# Revit family: Domotics-DomesticRanges-GEWISS-SYSTEM_COMMAND-THREE-WAY_SWITCH
name_source: partatom
category: Apparecchi elettrici
revit_build: Autodesk Revit 2016 (Build: 20161004_0715(x64)
units: mm (PartAtom-declared; Revit-internal decimal feet)

## family parameters
Condiviso = Sì
Host = Superficie
Mantenere orientamento annotazione = Sì
Numero OmniClass = 23.80.50.11.14
Punto di calcolo locali = Sì
Quota connettore circolare = Usa diametro
Taglio con vuoti quando caricato = No
Tipo di parte = Normale
Titolo OmniClass = Switches

## types (5) — shared parameters
Bidimensionale = bidimensionale system commutatori : simboli
Carico apparente = 0 VA
Catalogue = DOMOTICS
Catalogue Range = SYSTEM - DOMESTIC RANGE
Description. = Three-way switch
Electrocod = 0130
IDF = dab08859-5c6b-41ac-be4a-f9753a63331f
IDT = c003c8fd-f059-4307-83ec-7b86c7d74ecb
Immagine tipo = GW21559.jpg
Larghezza pulsante = 23 mm  [stored 0.0754593 ft]
N. poli = 1
No. SYSTEM modules = 1
Produttore = GEWISS S.p.A.
Prospetto di default = 1219 mm
SEO = 3 way switch
Simbolo_ = SIMBOLO COMMUTATORI : COMM
Technical sheet = https://www.gewiss.com
Tipo_ = SYSTEM COMMUTATORI_BASE : GW21559 - Nero
URL = https://www.gewiss.com
Version file RFA = 19.4
Volt = 230 V

## per-type parameters (varying)
| type | Button key | Colour | Description: | Descrizione | EAN code | Modello | Type | Voltage | Voltage: |
| GW21559 - Black | Neutral | Black | 1P - 10AX | 3-WAY SWITCH 1-0-2 10A SY/BK | 8011564133082 | GW21559 | 1P | 250 V ac | 250 V ac |
| GW20559 - White | Neutral | White | 1P - 10AX | 3-WAY SWITCH 1-0-2 10A SY/WT | 8011564133006 | GW20559 | 1P | 250 V ac | 250 V ac |
| GW21528 - Black | With replaceable neutral lens | Black | 1P - 10AX | 3-WAY SWITCH 1-0-2 10A NEUT.DISCS SY/BK | 8011564128279 | GW21528 | 1P | 250 V ac | 250 V ac |
| GW20560 - White 2P | Neutral |  | 2P - 10AX | 3-WAY SWITCH 2P 1-0-2 SY/WH | 8011564818026 | GW20560 | 2P |  |  |
| GW20528 - White | With replaceable neutral lens | White | 1P - 10AX | 3-WAY SWITCH 1-0-2 10A NEUT.DISCS SY/WT | 8011564077409 | GW20528 | 1P | 250 V ac | 250 V ac |

note: [stored X ft] marks values corroborated as IEEE doubles in the binary element streams (Revit-internal decimal feet)

## geometry (parser evidence)
native form markers: Sweep x2
no freeform markers — native parametric forms only
